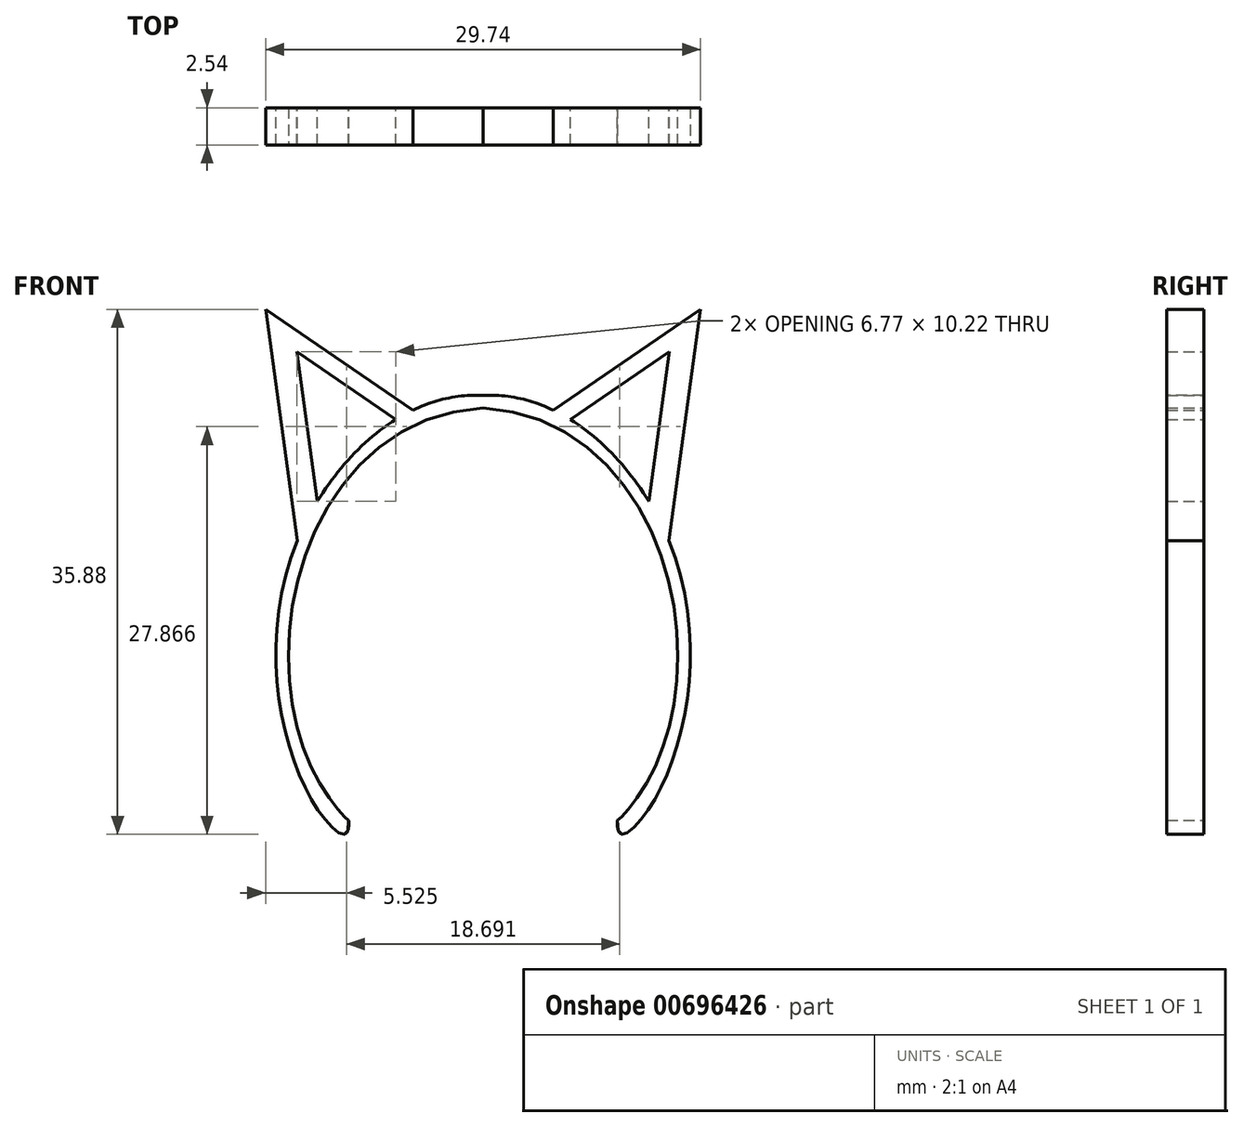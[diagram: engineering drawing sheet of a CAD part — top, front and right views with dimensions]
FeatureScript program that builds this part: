
annotation { "Feature Type Name" : "Feature", "Feature Type Description" : "" }
export const myFeature = defineFeature(function(context is Context, id is Id, definition is map)
    precondition{}
    {
        {
            var Q0;
            Q0=qCreatedBy(makeId("Front.planeOp"),FACE);
            var sketch = newSketch(context, id + "F0", { "sketchPlane" : qUnion([Q0])});
            skFitSpline(sketch, "E0", {"points": [v(0, 29.04) * mm, v(13.5, 16.72) * mm, v(10.76, 0) * mm, v(9.19, 0) * mm], "startDerivative": vector(41.12, 2.4) * mm, "endDerivative": vector(2.35, 36.13) * mm});
            skFitSpline(sketch, "E1.MirrorCS", {"points": [v(0, 29.04) * mm, v(-13.5, 16.72) * mm, v(-10.76, 0) * mm, v(-9.19, 0) * mm], "startDerivative": vector(-41.12, 2.4) * mm, "endDerivative": vector(-2.35, 36.13) * mm});
            skLineSegment(sketch, "E2", {"start": v(4.79, 28.04) * mm, "end": v(14.87, 34.92) * mm});
            skLineSegment(sketch, "E3", {"start": v(14.87, 34.92) * mm, "end": v(12.69, 19.1) * mm});
            skLineSegment(sketch, "E4.MirrorCS", {"start": v(-4.79, 28.04) * mm, "end": v(-14.87, 34.92) * mm});
            skLineSegment(sketch, "E5.MirrorCS", {"start": v(-14.87, 34.92) * mm, "end": v(-12.69, 19.1) * mm});
            skLineSegment(sketch, "E6", {"start": v(5.96, 27.4) * mm, "end": v(12.73, 32.02) * mm});
            skLineSegment(sketch, "E7", {"start": v(12.73, 32.02) * mm, "end": v(11.32, 21.8) * mm});
            skLineSegment(sketch, "E8.MirrorCS", {"start": v(-5.96, 27.4) * mm, "end": v(-12.73, 32.02) * mm});
            skLineSegment(sketch, "E9.MirrorCS", {"start": v(-12.73, 32.02) * mm, "end": v(-11.32, 21.8) * mm});
            skFitSpline(sketch, "E10", {"points": [v(0, 28.2) * mm, v(12.45, 17.22) * mm, v(11.68, 3.49) * mm, v(9.19, 0) * mm, v(9.15, 0) * mm], "startDerivative": vector(49.92, -3.1) * mm, "endDerivative": vector(-1.4, 1) * mm});
            skFitSpline(sketch, "E11.MirrorCS", {"points": [v(0, 28.2) * mm, v(-12.45, 17.22) * mm, v(-11.68, 3.49) * mm, v(-9.19, 0) * mm, v(-9.15, 0) * mm], "startDerivative": vector(-49.92, -3.1) * mm, "endDerivative": vector(1.4, 1) * mm});
            skSolve(sketch);
        }
        {
            var Q0;
            {var subQ0=sQuery(id+"F0.wireOp",EDGE,"E2");Q0=makeQuery(id+"F0.imprint","IMPRINT",FACE,{"disambiguationData":[TD([[makeQuery(id+"F0.imprint","IMPRINT",EDGE,{"derivedFrom":subQ0}),-1.0]])]});}
            var Q1;
            {var subQ3=sQuery(id+"F0.wireOp",EDGE,"E4.MirrorCS");Q1=makeQuery(id+"F0.imprint","IMPRINT",FACE,{"disambiguationData":[TD([[makeQuery(id+"F0.imprint","IMPRINT",EDGE,{"derivedFrom":subQ3}),1.0]])]});}
            var Q2;
            {var subQ0=sQuery(id+"F0.wireOp",EDGE,"E1.MirrorCS");var subQ4=sQuery(id+"F0.wireOp",EDGE,"E0");var subQ5=makeQuery(id+"F0.imprint","INTERSECT",VERTEX,{"derivedFrom":[subQ4,subQ0]});Q2=makeQuery(id+"F0.imprint","IMPRINT",FACE,{"disambiguationData":[TD([[makeQuery(id+"F0.imprint","IMPRINT",EDGE,{"disambiguationData":[TD([[subQ5,-1.0]])],"derivedFrom":subQ4}),-1.0]])]});}
            extrude(context, id + "F1", {"entities" : qUnion([Q0, Q1, Q2]), "depth" : 2.54 * mm, "offsetDistance" : 25.4 * mm});
        }
    });
